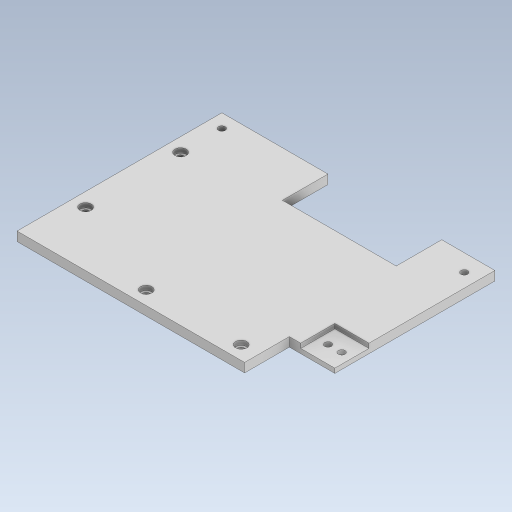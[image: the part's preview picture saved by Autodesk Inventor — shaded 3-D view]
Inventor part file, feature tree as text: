
AUTODESK INVENTOR PART (.ipt)
format: ipt  version: 2023.5 (Build 275446000, 446)  size: 156,160 bytes
history: native  units: in
note: dims shown in document units (in); Inventor stores cm internally (conversion verified against a paired STEP export)
features: extrude x2, sketch x1
ambient origin geometry x8: Origin, YZ Plane, XZ Plane, XY Plane, X Axis, Y Axis, Z Axis, Center Point
bodies: Solid1 (feature_tree)
feature tree (3):
  sketch  "Sketch1"  dims[d0=0.1575in d1=0.0in d2=0.0787in d3=0.0in d4=0.4724in d5=0.2953in d6=0.4724in d7=0.3543in d8=0.0in d10=0.0in d11=0.1969in]
  extrude  "Extrusion1"  Depth=0.0787in TaperAngle=0.0deg
  extrude  "Extrusion2"  Depth=0.1969in
